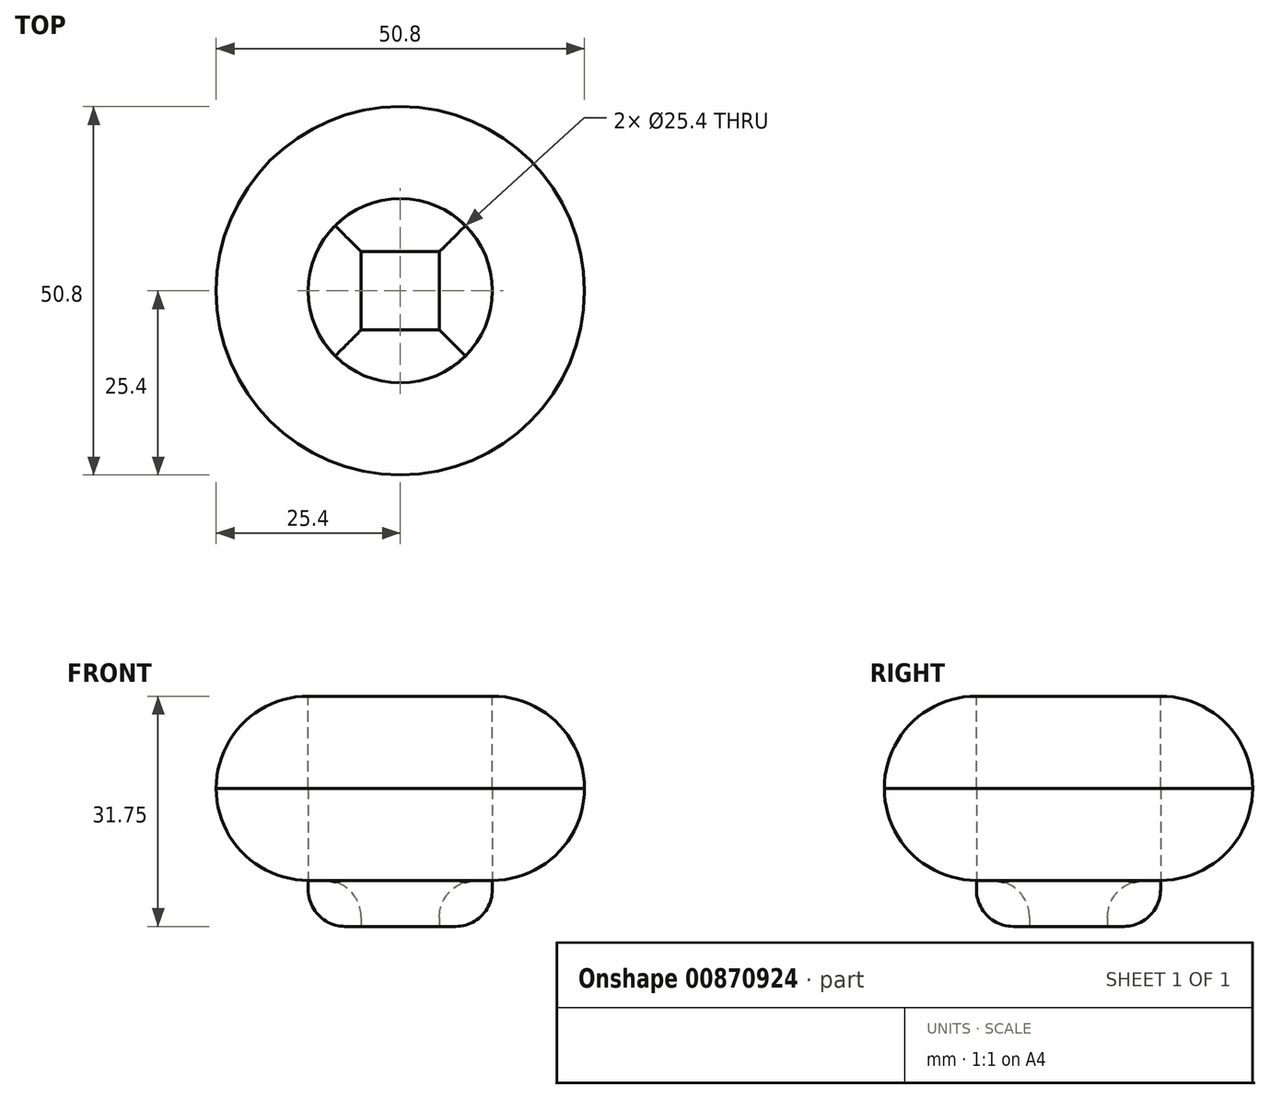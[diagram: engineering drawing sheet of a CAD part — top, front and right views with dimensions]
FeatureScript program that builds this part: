
annotation { "Feature Type Name" : "Feature", "Feature Type Description" : "" }
export const myFeature = defineFeature(function(context is Context, id is Id, definition is map)
    precondition{}
    {
        {
            var Q0;
            Q0=qCreatedBy(makeId("Top.planeOp"),FACE);
            var sketch = newSketch(context, id + "F0", { "sketchPlane" : qUnion([Q0])});
            skCircle(sketch, "E0", {"center": v(0, 0) * mm, "radius": 12.7 * mm});
            skCircle(sketch, "E1", {"center": v(0, 0) * mm, "radius": 7.62 * mm});
            skLineSegment(sketch, "E2.bottom", {"start": v(5.39, -5.39) * mm, "end": v(-5.39, -5.39) * mm});
            skLineSegment(sketch, "E2.top", {"start": v(5.39, 5.39) * mm, "end": v(-5.39, 5.39) * mm});
            skLineSegment(sketch, "E2.left", {"start": v(5.39, -5.39) * mm, "end": v(5.39, 5.39) * mm});
            skLineSegment(sketch, "E2.right", {"start": v(-5.39, -5.39) * mm, "end": v(-5.39, 5.39) * mm});
            skSolve(sketch);
        }
        {
            var Q0;
            Q0=makeQuery(id+"F0.imprint","IMPRINT",FACE,{"disambiguationData":[TD([[makeQuery(id+"F0.imprint","IMPRINT",EDGE,{"derivedFrom":sQuery(id+"F0.wireOp",EDGE,"E0")}),1.0]])]});
            var Q1;
            {var subQ0=sQuery(id+"F0.wireOp",EDGE,"E2.bottom");Q1=makeQuery(id+"F0.imprint","IMPRINT",FACE,{"disambiguationData":[TD([[makeQuery(id+"F0.imprint","IMPRINT",EDGE,{"derivedFrom":subQ0}),1.0]])]});}
            var Q2;
            {var subQ0=sQuery(id+"F0.wireOp",EDGE,"E2.right");Q2=makeQuery(id+"F0.imprint","IMPRINT",FACE,{"disambiguationData":[TD([[makeQuery(id+"F0.imprint","IMPRINT",EDGE,{"derivedFrom":subQ0}),1.0]])]});}
            var Q3;
            {var subQ0=sQuery(id+"F0.wireOp",EDGE,"E2.left");Q3=makeQuery(id+"F0.imprint","IMPRINT",FACE,{"disambiguationData":[TD([[makeQuery(id+"F0.imprint","IMPRINT",EDGE,{"derivedFrom":subQ0}),-1.0]])]});}
            var Q4;
            {var subQ0=sQuery(id+"F0.wireOp",EDGE,"E2.top");Q4=makeQuery(id+"F0.imprint","IMPRINT",FACE,{"disambiguationData":[TD([[makeQuery(id+"F0.imprint","IMPRINT",EDGE,{"derivedFrom":subQ0}),-1.0]])]});}
            extrude(context, id + "F1", {"entities" : qUnion([Q0, Q1, Q2, Q3, Q4]), "depth" : 6.35 * mm, "offsetDistance" : 25.4 * mm});
        }
        {
            var Q0;
            Q0=makeQuery(id+"F1.opExtrude","CAP_FACE",FACE,{"disambiguationData":[OSD([sQuery(id+"F0.wireOp",EDGE,"E0"),sQuery(id+"F0.wireOp",EDGE,"E1")])],"isStart":false});
            var sketch = newSketch(context, id + "F2", { "sketchPlane" : qUnion([Q0])});
            skCircle(sketch, "E3", {"center": v(0, 0) * mm, "radius": 25.4 * mm});
            skSolve(sketch);
        }
        {
            var Q0;
            Q0=makeQuery(id+"F2.imprint","IMPRINT",FACE,{"disambiguationData":[TD([[makeQuery(id+"F2.imprint","IMPRINT",EDGE,{"derivedFrom":sQuery(id+"F2.wireOp",EDGE,"E3")}),1.0]])]});
            extrude(context, id + "F3", {"entities" : qUnion([Q0]), "depth" : 12.7 * mm, "offsetDistance" : 25.4 * mm});
        }
        {
            var Q0;
            Q0=makeQuery(id+"F3.opExtrude","CAP_EDGE",EDGE,{"disambiguationData":[OSD([sQuery(id+"F2.wireOp",EDGE,"E3")])],"isStart":true});
            fillet(context, id + "F4", {"entities" : qUnion([Q0]), "radius" : 12.7 * mm, "tangentPropagation" : true, "allowEdgeOverflow" : false});
        }
        {
            var Q0;
            Q0=makeQuery(id+"F1.opExtrude","CAP_EDGE",EDGE,{"disambiguationData":[OSD([sQuery(id+"F0.wireOp",EDGE,"E0")])],"isStart":true});
            fillet(context, id + "F5", {"entities" : qUnion([Q0]), "radius" : 5.08 * mm, "tangentPropagation" : true, "allowEdgeOverflow" : false});
        }
        {
            var Q0;
            Q0=makeQuery(id+"F1.opExtrude","CAP_EDGE",EDGE,{"disambiguationData":[OSD([sQuery(id+"F0.wireOp",EDGE,"E2.left")])],"isStart":false});
            var Q1;
            Q1=makeQuery(id+"F1.opExtrude","CAP_EDGE",EDGE,{"disambiguationData":[OSD([sQuery(id+"F0.wireOp",EDGE,"E2.bottom")])],"isStart":false});
            var Q2;
            Q2=makeQuery(id+"F1.opExtrude","CAP_EDGE",EDGE,{"disambiguationData":[OSD([sQuery(id+"F0.wireOp",EDGE,"E2.right")])],"isStart":false});
            var Q3;
            Q3=makeQuery(id+"F1.opExtrude","CAP_EDGE",EDGE,{"disambiguationData":[OSD([sQuery(id+"F0.wireOp",EDGE,"E2.top")])],"isStart":false});
            fillet(context, id + "F6", {"entities" : qUnion([Q0, Q1, Q2, Q3]), "radius" : 5.08 * mm, "tangentPropagation" : true, "allowEdgeOverflow" : false});
        }
        {
            var Q0;
            Q0=makeQuery(id+"F3.opExtrude","SWEPT_BODY",BODY,{"disambiguationData":[OSD([sQuery(id+"F0.wireOp",EDGE,"E0"),sQuery(id+"F2.wireOp",EDGE,"E3")])]});
            var Q1;
            Q1=makeQuery(id+"F3.opExtrude","CAP_FACE",FACE,{"disambiguationData":[OSD([sQuery(id+"F0.wireOp",EDGE,"E0"),sQuery(id+"F2.wireOp",EDGE,"E3")])],"isStart":false});
            mirror(context, id + "F7", {"operationType" : NewBodyOperationType.ADD, "entities" : qUnion([Q0]), "mirrorPlane" : qUnion([Q1])});
        }
    });
